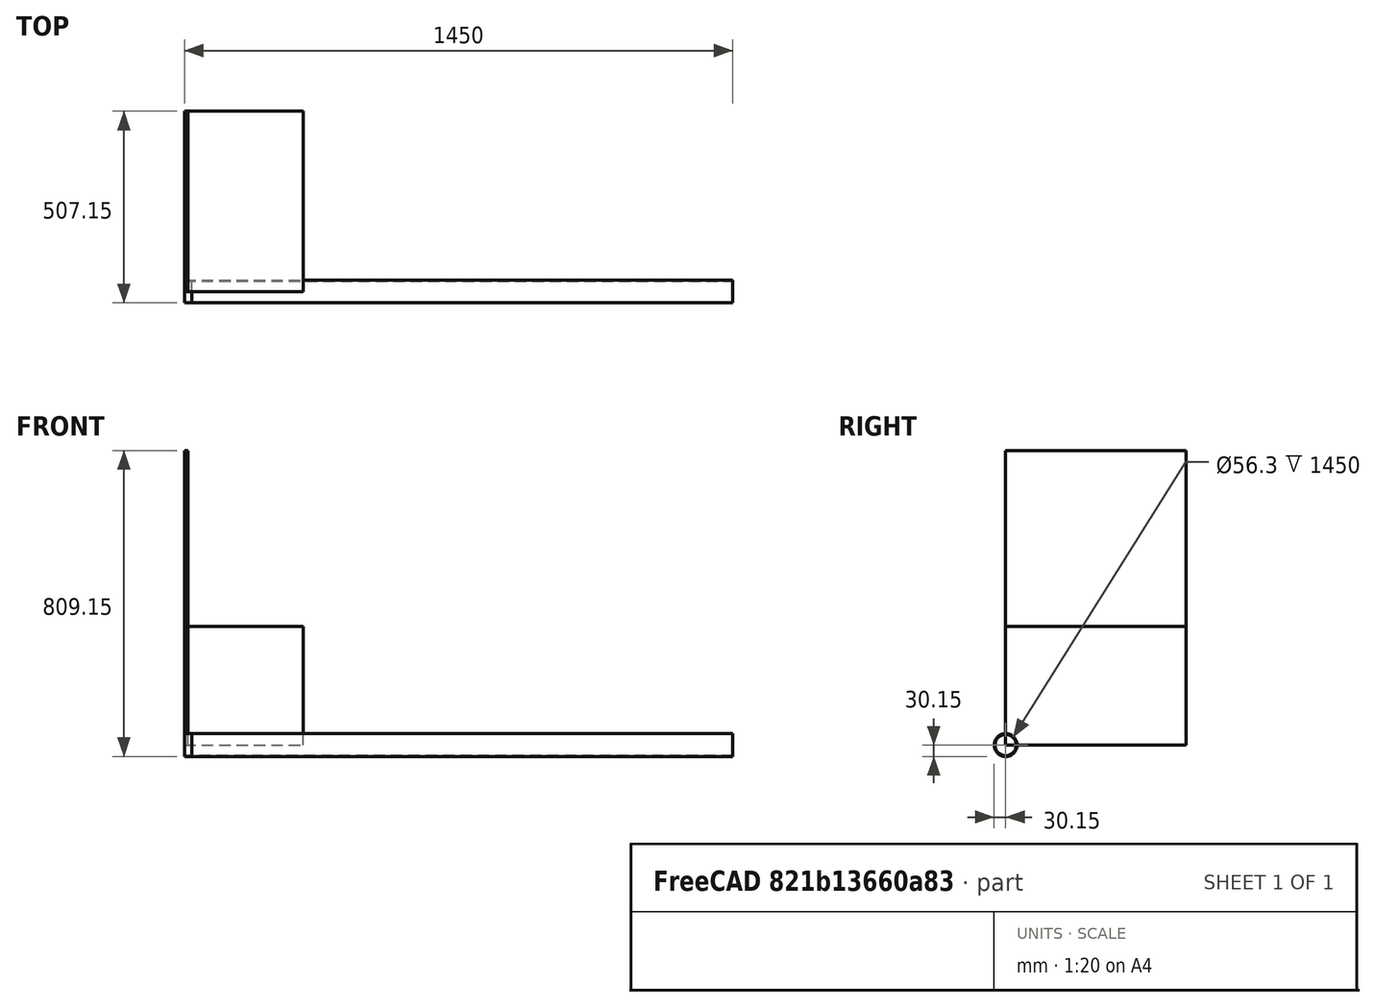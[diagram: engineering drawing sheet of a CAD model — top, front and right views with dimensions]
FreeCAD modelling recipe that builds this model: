
FCSTD DOCUMENT  (FreeCAD 0.18.4R)
Label: intercambiador_v2
License: All rights reserved
LicenseURL: http://en.wikipedia.org/wiki/All_rights_reserved
objects: Part::Box×2, Sketcher::SketchObject×1, PartDesign::Pad×1, PartDesign::Body×1, Part::Cylinder×1
note: 7 computed .brp shape members not serialized (recipe doc carries the construction recipe); baked Part::Feature solids carry a one-line shape summary decoded from their .brp

FEATURE [Sketcher::SketchObject] Sketch
  MapMode = 5
  Placement = pos=(0,0,0) rot=(0.57735,0.57735,0.57735;2.0944rad)
  Support = -> [YZ_Plane]
  sketch-geometry (2):
    g0: Circle CenterX=0 CenterY=0 CenterZ=0 NormalX=0 NormalY=0 NormalZ=1 AngleXU=0 Radius=30.15
    g1: Circle CenterX=0 CenterY=0 CenterZ=0 NormalX=0 NormalY=0 NormalZ=1 AngleXU=0 Radius=28.15
  constraints (2):
    c: Diameter(g0) = 60.3
    c: Diameter(g1) = 56.3
FEATURE [PartDesign::Pad] Pad
  Length = 1450
  Length2 = 100
  Placement = pos=(0,0,0) rot=(0.57735,0.57735,0.57735;2.0944rad)
  Profile = -> Sketch
  Type = 0
FEATURE [PartDesign::Body] Body  label="Caños"
  Group = -> [Sketch,Pad]
  Origin = -> Origin
  Tip = -> Pad
FEATURE [Part::Cylinder] Cylinder  label="Cilindro"
  Angle = 360
  AttacherType = Attacher::AttachEngine3D
  Height = 20
  Placement = pos=(0,0,0) rot=(0,1,0;1.5708rad)
  Radius = 30.15
FEATURE [Part::Box] Box  label="Chapa tubos"
  AttacherType = Attacher::AttachEngine3D
  Height = 779
  Length = 0
  Width = 477
FEATURE [Part::Box] Box001  label="Placa separadora"
  AttacherType = Attacher::AttachEngine3D
  Height = 314
  Length = 0
  Width = 477
